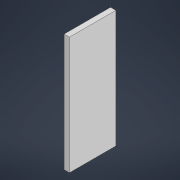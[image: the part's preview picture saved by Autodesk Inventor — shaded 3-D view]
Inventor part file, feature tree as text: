
AUTODESK INVENTOR PART (.ipt)
format: ipt  version: 2022 (Build 260153000, 153)  size: 86,528 bytes
history: native  units: mm
features: extrude x1, sketch x1
ambient origin geometry x8: Origin, YZ Plane, XZ Plane, XY Plane, X Axis, Y Axis, Z Axis, Center Point
bodies: Body1 (feature_tree)
feature tree (2):
  extrude  "Выдавливание2"  Depth=266.0mm
  sketch  "Эскиз2"
